# Revit family: Hager-PABLO-Flush_mounted-IP40-With_Cover-With_DIN-NoHosted-IT-it
name_source: partatom
category: Electrical Equipment
units: mm (PartAtom-declared; Revit-internal decimal feet)

## family parameters
Always vertical = Yes
Cut with Voids When Loaded = No
Maintain Annotation Orientation = No
Panel Configuration = Two Columns, Circuits Across
Part Type = Panelboard
Room Calculation Point = No
Round Connector Dimension = Use Diameter
Shared = No
Work Plane-Based = Yes

## types (18) — shared parameters
Code hager = ADD-EC000214_EU
Default Elevation = 1200 mm
EF000003 - Tipo di montaggio = Incassato
EF000024 - Resistente ai raggi UV = No
EF000118 - Con piastra di montaggio = No
EF001062 - Esecuzione EMC = No
EF001088 - Possibilità di applicazione = No
EF001134 - Barra DIN = Yes
EF005474 - Grado di protezione (IP) = IP40
EF006306 - Con serratura = No
EF015776 - Morsettiera di terra = No
EF015777 - Morsettiera neutra = No
EF015941 - Segnale di passaggio porta = No
ETIM class code = EC000214
ETIM class name = Small distribution board
HG000002-with door or cover-it = Yes
HG000003-Range-it = PABLO
HG000005-Thickness-it = 2 mm  [stored 0.00656168 ft]
HG000006-Flush mounted-it = Yes
HG000009-Double swing door-it = No
HG000010-Asymmetric doors-it = No
HG000011-Empty rows from bottom-it = No
HG000012-Door swing angle-it = 90.00°
HG000013-Door on the left-it = No
HG000014-Door on the right-it = Yes
HG000015-Clearance visibility-it = Yes
HG000016-Door 3D visibility-it = Yes
HG000017-Distance between poles-it = 18 mm  [stored 0.0590551 ft]
HG000099-Onfly Template ID-it-IT = 507532
Manufacturer = Hager
Name BIM&CO = Electricity
Name hager = ADD_Enclosures_EC000214
Reference = Template-Enclosure_EU-EC000214
Uniformat = Low Tension Service & Dist.
Uniformat code = D501001
zero-valued in all types: EF001131 - Profondità interna, HG000001 - Numero di colonne, HG000007-Number of empty columns-it, HG000008-Number of empty rows-it

## per-type parameters (varying)
| type | BC_METADATA | EF000008 - Larghezza | EF000040 - Altezza | EF000049 - Profondità | EF000116 - Numero RAL | EF000218 - Profondità di incasso | EF000266 - Numero di file | EF000332 - Altezza della parte incassata | EF000846 - Larghezza di montaggio | EF002950 - Numero moduli DIN | EF006244 - Coperchio/porta trasparente | HG000004-Manufacturer reference-it | HG000060-RAL-number | HGEF000266-Numero di file | HGEF0002950-Numero moduli DIN |
| PABLO-Flush_mounted_W345_H425_D109_12_Modular_Spacing-B04104 | {"ObjectGuid":"2a0cc614-8ccd-46e7-b0f1-7b8e4291b305","ModelGuid":"4fddb95c-943d-4a19-9faf-58cc779e7682","VariantGuid":"d0a759b0-f4a8-4738-b515-9f91f7cdd338","Revision":"#6","VariantName":"PABLO-Flush_mounted_W345_H425_D109_12_Modular_Spacing-B04104"} | 345 mm  [stored 1.13189 ft] | 425 mm  [stored 1.39436 ft] | 109 mm  [stored 0.357612 ft] | 9016 | 77 mm  [stored 0.252625 ft] | 2 | 405 mm  [stored 1.32874 ft] | 345 mm  [stored 1.13189 ft] | 12 | No | B04104 | 9016 | 2 | 12 |
| PABLO-Flush_mounted_W455_H475_D114_12_Modular_Spacing-B04105 | {"ObjectGuid":"2a0cc614-8ccd-46e7-b0f1-7b8e4291b305","ModelGuid":"4fddb95c-943d-4a19-9faf-58cc779e7682","VariantGuid":"68bf7635-be27-4574-8cf1-d07818dea149","Revision":"#6","VariantName":"PABLO-Flush_mounted_W455_H475_D114_12_Modular_Spacing-B04105"} | 455 mm | 475 mm  [stored 1.5584 ft] | 114 mm  [stored 0.374016 ft] | 9016 | 77 mm  [stored 0.252625 ft] | 2 | 455 mm | 455 mm | 12 | No | B04105 | 9016 | 2 | 12 |
| PABLO-Flush_mounted_W175_H191_D25_0_Modular_Spacing-B04941 | {"ObjectGuid":"2a0cc614-8ccd-46e7-b0f1-7b8e4291b305","ModelGuid":"4fddb95c-943d-4a19-9faf-58cc779e7682","VariantGuid":"f8ae05e7-7d22-488d-8c00-bb9b22f0254a","Revision":"#6","VariantName":"PABLO-Flush_mounted_W175_H191_D25_0_Modular_Spacing-B04941"} | 175 mm  [stored 0.574147 ft] | 191 mm  [stored 0.62664 ft] | 25 mm  [stored 0.082021 ft] | 0 | 16 mm  [stored 0.0524934 ft] | 0 | 160 mm  [stored 0.524934 ft] | 175 mm  [stored 0.574147 ft] | 0 | No | B04941 | 0 | 0 | 0 |
| PABLO-Flush_mounted_W211_H191_D25_0_Modular_Spacing-B04942 | {"ObjectGuid":"2a0cc614-8ccd-46e7-b0f1-7b8e4291b305","ModelGuid":"4fddb95c-943d-4a19-9faf-58cc779e7682","VariantGuid":"1a511315-7559-42e8-87d4-9b78164af7ee","Revision":"#6","VariantName":"PABLO-Flush_mounted_W211_H191_D25_0_Modular_Spacing-B04942"} | 211 mm  [stored 0.692257 ft] | 191 mm  [stored 0.62664 ft] | 25 mm  [stored 0.082021 ft] | 9016 | 16 mm  [stored 0.0524934 ft] | 0 | 160 mm  [stored 0.524934 ft] | 211 mm  [stored 0.692257 ft] | 0 | No | B04942 | 9016 | 0 | 0 |
| PABLO-Flush_mounted_W280_H235_D25_0_Modular_Spacing-B04943 | {"ObjectGuid":"2a0cc614-8ccd-46e7-b0f1-7b8e4291b305","ModelGuid":"4fddb95c-943d-4a19-9faf-58cc779e7682","VariantGuid":"63e16b07-1304-41dc-b4d2-54931c352868","Revision":"#6","VariantName":"PABLO-Flush_mounted_W280_H235_D25_0_Modular_Spacing-B04943"} | 280 mm  [stored 0.918635 ft] | 235 mm  [stored 0.770997 ft] | 25 mm  [stored 0.082021 ft] | 0 | 16 mm  [stored 0.0524934 ft] | 0 | 160 mm  [stored 0.524934 ft] | 280 mm  [stored 0.918635 ft] | 0 | No | B04943 | 0 | 0 | 0 |
| PABLO-Flush_mounted_W352_H275_D25_12_Modular_Spacing-B04944 | {"ObjectGuid":"2a0cc614-8ccd-46e7-b0f1-7b8e4291b305","ModelGuid":"4fddb95c-943d-4a19-9faf-58cc779e7682","VariantGuid":"38bd699e-2bfe-4431-8154-4ddebf2d1a15","Revision":"#6","VariantName":"PABLO-Flush_mounted_W352_H275_D25_12_Modular_Spacing-B04944"} | 352 mm  [stored 1.15486 ft] | 275 mm | 25 mm  [stored 0.082021 ft] | 9016 | 16 mm  [stored 0.0524934 ft] | 1 | 160 mm  [stored 0.524934 ft] | 352 mm  [stored 1.15486 ft] | 12 | No | B04944 | 9016 | 1 | 12 |
| PABLO-Flush_mounted_W460_H275_D25_18_Modular_Spacing-B04945 | {"ObjectGuid":"2a0cc614-8ccd-46e7-b0f1-7b8e4291b305","ModelGuid":"4fddb95c-943d-4a19-9faf-58cc779e7682","VariantGuid":"efdca5af-6dd7-4c6c-960d-ea80e91ee410","Revision":"#6","VariantName":"PABLO-Flush_mounted_W460_H275_D25_18_Modular_Spacing-B04945"} | 460 mm  [stored 1.50919 ft] | 275 mm | 25 mm  [stored 0.082021 ft] | 9016 | 16 mm  [stored 0.0524934 ft] | 1 | 160 mm  [stored 0.524934 ft] | 460 mm  [stored 1.50919 ft] | 18 | No | B04945 | 9016 | 1 | 18 |
| PABLO-Flush_mounted_W352_H425_D25_12_Modular_Spacing-B04946 | {"ObjectGuid":"2a0cc614-8ccd-46e7-b0f1-7b8e4291b305","ModelGuid":"4fddb95c-943d-4a19-9faf-58cc779e7682","VariantGuid":"54bf27ca-efac-4af1-8742-6c2701148a03","Revision":"#6","VariantName":"PABLO-Flush_mounted_W352_H425_D25_12_Modular_Spacing-B04946"} | 352 mm  [stored 1.15486 ft] | 425 mm  [stored 1.39436 ft] | 25 mm  [stored 0.082021 ft] | 9016 | 16 mm  [stored 0.0524934 ft] | 2 | 405 mm  [stored 1.32874 ft] | 352 mm  [stored 1.15486 ft] | 12 | No | B04946 | 9016 | 2 | 12 |
| PABLO-Flush_mounted_W352_H575_D25_12_Modular_Spacing-B04947 | {"ObjectGuid":"2a0cc614-8ccd-46e7-b0f1-7b8e4291b305","ModelGuid":"4fddb95c-943d-4a19-9faf-58cc779e7682","VariantGuid":"6db7cb3e-69b2-49d6-a8cc-02b7af286175","Revision":"#6","VariantName":"PABLO-Flush_mounted_W352_H575_D25_12_Modular_Spacing-B04947"} | 352 mm  [stored 1.15486 ft] | 575 mm | 25 mm  [stored 0.082021 ft] | 9016 | 16 mm  [stored 0.0524934 ft] | 3 | 405 mm  [stored 1.32874 ft] | 352 mm  [stored 1.15486 ft] | 12 | No | B04947 | 9016 | 3 | 12 |
| PABLO-Flush_mounted_W460_H575_D25_18_Modular_Spacing-B04948 | {"ObjectGuid":"2a0cc614-8ccd-46e7-b0f1-7b8e4291b305","ModelGuid":"4fddb95c-943d-4a19-9faf-58cc779e7682","VariantGuid":"1864942c-5e8d-467c-8965-4e9db0fd6af0","Revision":"#6","VariantName":"PABLO-Flush_mounted_W460_H575_D25_18_Modular_Spacing-B04948"} | 460 mm  [stored 1.50919 ft] | 575 mm | 25 mm  [stored 0.082021 ft] | 9016 | 16 mm  [stored 0.0524934 ft] | 3 | 405 mm  [stored 1.32874 ft] | 460 mm  [stored 1.50919 ft] | 18 | No | B04948 | 9016 | 3 | 18 |
| PABLO-Flush_mounted_W175_H191_D25_0_Modular_Spacing-B04951 | {"ObjectGuid":"2a0cc614-8ccd-46e7-b0f1-7b8e4291b305","ModelGuid":"4fddb95c-943d-4a19-9faf-58cc779e7682","VariantGuid":"d37d6247-f035-4e03-92b8-f2be67cb451b","Revision":"#6","VariantName":"PABLO-Flush_mounted_W175_H191_D25_0_Modular_Spacing-B04951"} | 175 mm  [stored 0.574147 ft] | 191 mm  [stored 0.62664 ft] | 25 mm  [stored 0.082021 ft] | 9016 | 16 mm  [stored 0.0524934 ft] | 0 | 160 mm  [stored 0.524934 ft] | 175 mm  [stored 0.574147 ft] | 0 | No | B04951 | 9016 | 0 | 0 |
| PABLO-Flush_mounted_W211_H191_D25_0_Modular_Spacing-B04952 | {"ObjectGuid":"2a0cc614-8ccd-46e7-b0f1-7b8e4291b305","ModelGuid":"4fddb95c-943d-4a19-9faf-58cc779e7682","VariantGuid":"da64da52-9e45-4a0c-b1bc-2abe69471082","Revision":"#6","VariantName":"PABLO-Flush_mounted_W211_H191_D25_0_Modular_Spacing-B04952"} | 211 mm  [stored 0.692257 ft] | 191 mm  [stored 0.62664 ft] | 25 mm  [stored 0.082021 ft] | 0 | 16 mm  [stored 0.0524934 ft] | 0 | 160 mm  [stored 0.524934 ft] | 211 mm  [stored 0.692257 ft] | 0 | No | B04952 | 0 | 0 | 0 |
| PABLO-Flush_mounted_W280_H235_D25_0_Modular_Spacing-B04953 | {"ObjectGuid":"2a0cc614-8ccd-46e7-b0f1-7b8e4291b305","ModelGuid":"4fddb95c-943d-4a19-9faf-58cc779e7682","VariantGuid":"04f6d75d-a5db-4a7d-9b06-88772c7f0458","Revision":"#6","VariantName":"PABLO-Flush_mounted_W280_H235_D25_0_Modular_Spacing-B04953"} | 280 mm  [stored 0.918635 ft] | 235 mm  [stored 0.770997 ft] | 25 mm  [stored 0.082021 ft] | 0 | 16 mm  [stored 0.0524934 ft] | 0 | 160 mm  [stored 0.524934 ft] | 280 mm  [stored 0.918635 ft] | 0 | No | B04953 | 0 | 0 | 0 |
| PABLO-Flush_mounted_W352_H275_D25_12_Modular_Spacing-B04954 | {"ObjectGuid":"2a0cc614-8ccd-46e7-b0f1-7b8e4291b305","ModelGuid":"4fddb95c-943d-4a19-9faf-58cc779e7682","VariantGuid":"9aff3c40-16b7-444d-9749-3d02937ebfa8","Revision":"#6","VariantName":"PABLO-Flush_mounted_W352_H275_D25_12_Modular_Spacing-B04954"} | 352 mm  [stored 1.15486 ft] | 275 mm | 25 mm  [stored 0.082021 ft] | 7031 | 16 mm  [stored 0.0524934 ft] | 1 | 160 mm  [stored 0.524934 ft] | 352 mm  [stored 1.15486 ft] | 12 | Yes | B04954 | 7031 | 1 | 12 |
| PABLO-Flush_mounted_W460_H275_D25_18_Modular_Spacing-B04955 | {"ObjectGuid":"2a0cc614-8ccd-46e7-b0f1-7b8e4291b305","ModelGuid":"4fddb95c-943d-4a19-9faf-58cc779e7682","VariantGuid":"005ddf15-3d6e-415e-8efa-e8c4e5e456d6","Revision":"#6","VariantName":"PABLO-Flush_mounted_W460_H275_D25_18_Modular_Spacing-B04955"} | 460 mm  [stored 1.50919 ft] | 275 mm | 25 mm  [stored 0.082021 ft] | 7031 | 16 mm  [stored 0.0524934 ft] | 1 | 160 mm  [stored 0.524934 ft] | 460 mm  [stored 1.50919 ft] | 18 | No | B04955 | 7031 | 1 | 18 |
| PABLO-Flush_mounted_W352_H425_D25_12_Modular_Spacing-B04956 | {"ObjectGuid":"2a0cc614-8ccd-46e7-b0f1-7b8e4291b305","ModelGuid":"4fddb95c-943d-4a19-9faf-58cc779e7682","VariantGuid":"48c81d81-7748-4f12-a12d-f8632c246ebc","Revision":"#6","VariantName":"PABLO-Flush_mounted_W352_H425_D25_12_Modular_Spacing-B04956"} | 352 mm  [stored 1.15486 ft] | 425 mm  [stored 1.39436 ft] | 25 mm  [stored 0.082021 ft] | 7031 | 16 mm  [stored 0.0524934 ft] | 2 | 405 mm  [stored 1.32874 ft] | 352 mm  [stored 1.15486 ft] | 12 | Yes | B04956 | 7031 | 2 | 12 |
| PABLO-Flush_mounted_W352_H575_D25_12_Modular_Spacing-B04957 | {"ObjectGuid":"2a0cc614-8ccd-46e7-b0f1-7b8e4291b305","ModelGuid":"4fddb95c-943d-4a19-9faf-58cc779e7682","VariantGuid":"5eda7519-29e3-4116-9e22-2b3b6889a34a","Revision":"#6","VariantName":"PABLO-Flush_mounted_W352_H575_D25_12_Modular_Spacing-B04957"} | 352 mm  [stored 1.15486 ft] | 575 mm | 25 mm  [stored 0.082021 ft] | 7031 | 16 mm  [stored 0.0524934 ft] | 3 | 405 mm  [stored 1.32874 ft] | 352 mm  [stored 1.15486 ft] | 12 | No | B04957 | 7031 | 3 | 12 |
| PABLO-Flush_mounted_W460_H575_D25_18_Modular_Spacing-B04958 | {"ObjectGuid":"2a0cc614-8ccd-46e7-b0f1-7b8e4291b305","ModelGuid":"4fddb95c-943d-4a19-9faf-58cc779e7682","VariantGuid":"0cd62faf-5b9f-4e52-b711-824379da4e94","Revision":"#6","VariantName":"PABLO-Flush_mounted_W460_H575_D25_18_Modular_Spacing-B04958"} | 460 mm  [stored 1.50919 ft] | 575 mm | 25 mm  [stored 0.082021 ft] | 7031 | 16 mm  [stored 0.0524934 ft] | 3 | 405 mm  [stored 1.32874 ft] | 460 mm  [stored 1.50919 ft] | 18 | Yes | B04958 | 7031 | 3 | 18 |

note: [stored X ft] marks values corroborated as IEEE doubles in the binary element streams (Revit-internal decimal feet)

## geometry (parser evidence)
native form markers: Sweep x13
no freeform markers — native parametric forms only
